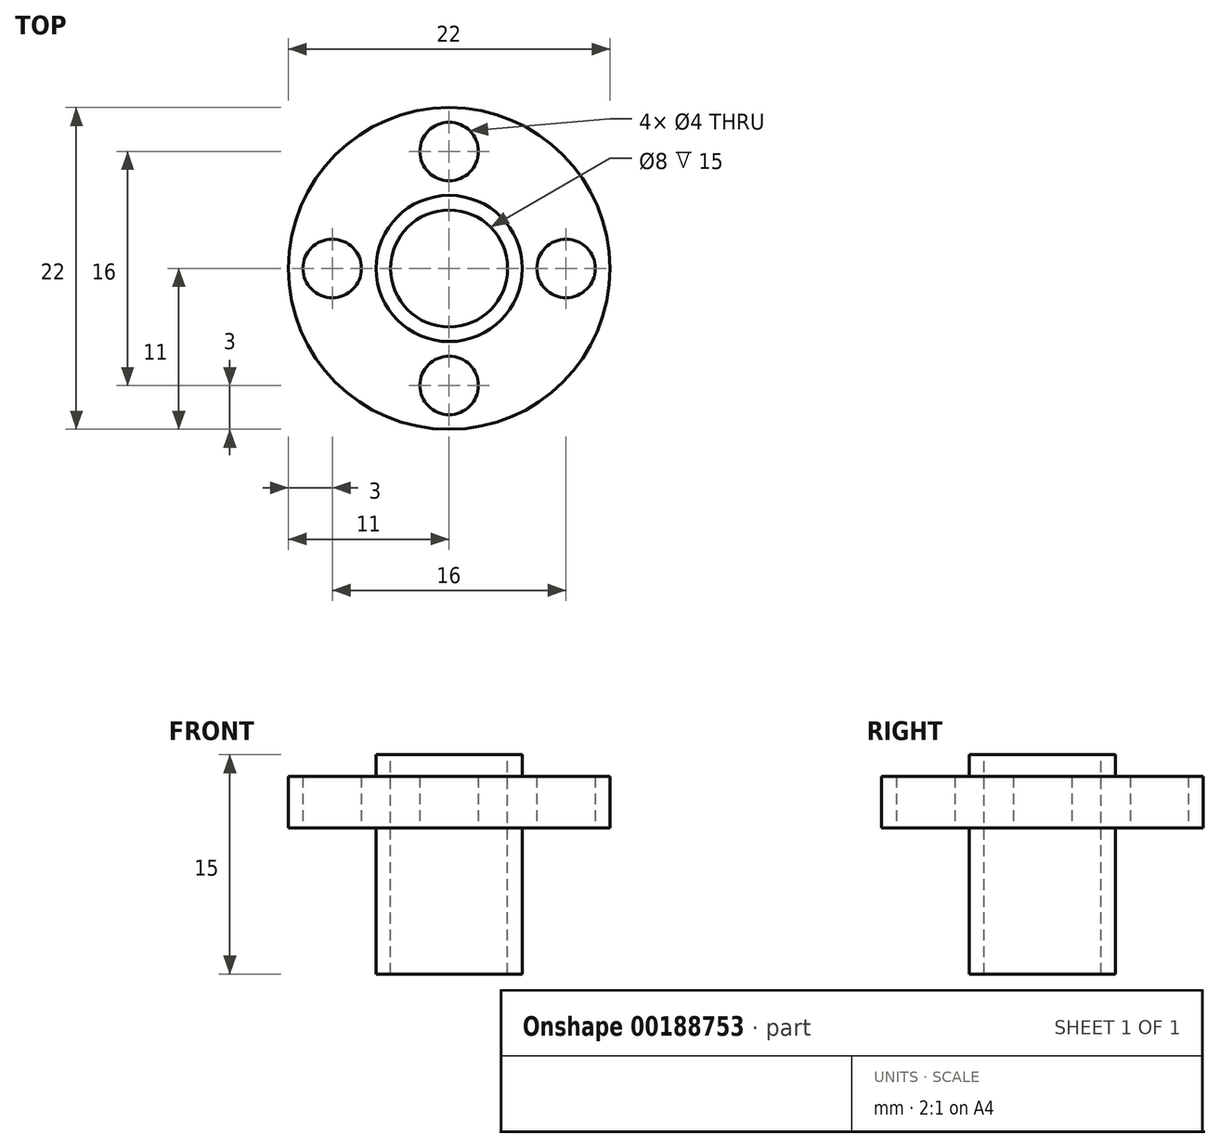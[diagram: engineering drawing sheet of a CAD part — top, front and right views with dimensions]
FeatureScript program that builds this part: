
annotation { "Feature Type Name" : "Feature", "Feature Type Description" : "" }
export const myFeature = defineFeature(function(context is Context, id is Id, definition is map)
    precondition{}
    {
        {
            var Q0;
            Q0=qCreatedBy(makeId("Top.planeOp"),FACE);
            var sketch = newSketch(context, id + "F0", { "sketchPlane" : qUnion([Q0])});
            skCircle(sketch, "E0", {"center": v(0, 0) * mm, "radius": 11 * mm});
            skCircle(sketch, "E1", {"center": v(0, 0) * mm, "radius": 8 * mm, "construction": true});
            skCircle(sketch, "E2", {"center": v(0, 8) * mm, "radius": 2 * mm});
            skCircle(sketch, "E3", {"center": v(-8, 0) * mm, "radius": 2 * mm});
            skCircle(sketch, "E4", {"center": v(0, -8) * mm, "radius": 2 * mm});
            skCircle(sketch, "E5", {"center": v(8, 0) * mm, "radius": 2 * mm});
            skSolve(sketch);
        }
        {
            var Q0;
            Q0=makeQuery(id+"F0.imprint","IMPRINT",FACE,{"disambiguationData":[TD([[makeQuery(id+"F0.imprint","IMPRINT",EDGE,{"derivedFrom":sQuery(id+"F0.wireOp",EDGE,"E0")}),1.0]])]});
            extrude(context, id + "F1", {"entities" : qUnion([Q0]), "depth" : 3.5 * mm});
        }
        {
            var Q0;
            Q0=makeQuery(id+"F1.opExtrude","CAP_FACE",FACE,{"disambiguationData":[OSD([sQuery(id+"F0.wireOp",EDGE,"E0")])],"isStart":false});
            var sketch = newSketch(context, id + "F2", { "sketchPlane" : qUnion([Q0])});
            skCircle(sketch, "E6", {"center": v(0, 0) * mm, "radius": 5 * mm});
            skSolve(sketch);
        }
        {
            var Q0;
            Q0=makeQuery(id+"F2.imprint","IMPRINT",FACE,{"disambiguationData":[TD([[makeQuery(id+"F2.imprint","IMPRINT",EDGE,{"derivedFrom":sQuery(id+"F2.wireOp",EDGE,"E6")}),1.0]])]});
            extrude(context, id + "F3", {"entities" : qUnion([Q0]), "operationType" : NewBodyOperationType.ADD, "depth" : 1.5 * mm});
        }
        {
            var Q0;
            Q0=makeQuery(id+"F1.opExtrude","CAP_FACE",FACE,{"disambiguationData":[OSD([sQuery(id+"F0.wireOp",EDGE,"E0")])],"isStart":true});
            var sketch = newSketch(context, id + "F4", { "sketchPlane" : qUnion([Q0])});
            skCircle(sketch, "E7", {"center": v(0, 0) * mm, "radius": 5 * mm});
            skSolve(sketch);
        }
        {
            var Q0;
            Q0=makeQuery(id+"F4.imprint","IMPRINT",FACE,{"disambiguationData":[TD([[makeQuery(id+"F4.imprint","IMPRINT",EDGE,{"derivedFrom":sQuery(id+"F4.wireOp",EDGE,"E7")}),1.0]])]});
            extrude(context, id + "F5", {"entities" : qUnion([Q0]), "operationType" : NewBodyOperationType.ADD, "depth" : 10 * mm});
        }
        {
            var Q0;
            Q0=makeQuery(id+"F3.opExtrude","CAP_FACE",FACE,{"disambiguationData":[OSD([sQuery(id+"F2.wireOp",EDGE,"E6")])],"isStart":false});
            var sketch = newSketch(context, id + "F6", { "sketchPlane" : qUnion([Q0])});
            skCircle(sketch, "E8", {"center": v(0, 0) * mm, "radius": 4 * mm});
            skSolve(sketch);
        }
        {
            var Q0;
            Q0=makeQuery(id+"F6.imprint","IMPRINT",FACE,{"disambiguationData":[TD([[makeQuery(id+"F6.imprint","IMPRINT",EDGE,{"derivedFrom":sQuery(id+"F6.wireOp",EDGE,"E8")}),1.0]])]});
            extrude(context, id + "F7", {"entities" : qUnion([Q0]), "operationType" : NewBodyOperationType.REMOVE, "endBound" : BoundingType.UP_TO_NEXT, "oppositeDirection" : true, "depth" : 25 * mm, "offsetDistance" : 25 * mm});
        }
    });
